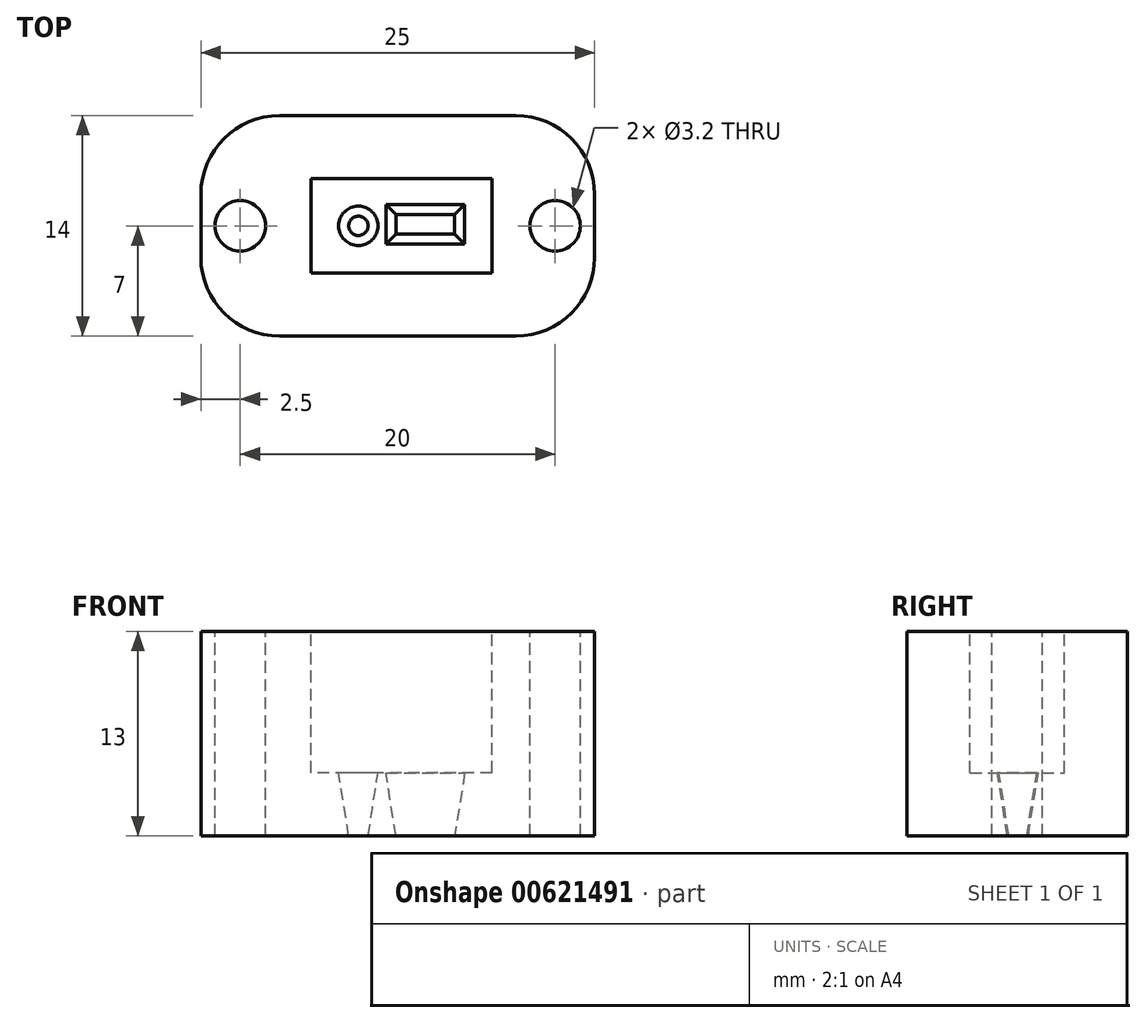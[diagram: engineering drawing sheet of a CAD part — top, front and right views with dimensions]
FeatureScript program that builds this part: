
annotation { "Feature Type Name" : "Feature", "Feature Type Description" : "" }
export const myFeature = defineFeature(function(context is Context, id is Id, definition is map)
    precondition{}
    {
        {
            var Q0;
            Q0=qCreatedBy(makeId("Top.planeOp"),FACE);
            var sketch = newSketch(context, id + "F0", { "sketchPlane" : qUnion([Q0])});
            skLineSegment(sketch, "E0.bottom", {"start": v(6, -3) * mm, "end": v(-5.5, -3) * mm});
            skLineSegment(sketch, "E0.top", {"start": v(6, 3) * mm, "end": v(-5.5, 3) * mm});
            skLineSegment(sketch, "E0.left", {"start": v(6, -3) * mm, "end": v(6, 3) * mm});
            skLineSegment(sketch, "E0.right", {"start": v(-5.5, -3) * mm, "end": v(-5.5, 3) * mm});
            skPoint(sketch, "E0.middle", {"position": v(1.75, 0.1) * mm});
            skLineSegment(sketch, "E1.bottom", {"start": v(12.5, -7) * mm, "end": v(-12.5, -7) * mm});
            skLineSegment(sketch, "E1.top", {"start": v(12.5, 7) * mm, "end": v(-12.5, 7) * mm});
            skLineSegment(sketch, "E1.left", {"start": v(12.5, -7) * mm, "end": v(12.5, 7) * mm});
            skLineSegment(sketch, "E1.right", {"start": v(-12.5, -7) * mm, "end": v(-12.5, 7) * mm});
            skCircle(sketch, "E2", {"center": v(10, 0) * mm, "radius": 1.6 * mm});
            skCircle(sketch, "E3", {"center": v(-10, 0) * mm, "radius": 1.6 * mm});
            skCircle(sketch, "E4", {"center": v(-2.5, 0) * mm, "radius": 1.25 * mm});
            skLineSegment(sketch, "E5.bottom", {"start": v(4.25, -1.16) * mm, "end": v(-0.75, -1.16) * mm});
            skLineSegment(sketch, "E5.top", {"start": v(4.25, 1.34) * mm, "end": v(-0.75, 1.34) * mm});
            skLineSegment(sketch, "E5.left", {"start": v(4.25, -1.16) * mm, "end": v(4.25, 1.34) * mm});
            skLineSegment(sketch, "E5.right", {"start": v(-0.75, -1.16) * mm, "end": v(-0.75, 1.34) * mm});
            skSolve(sketch);
        }
        {
            var Q0;
            Q0=makeQuery(id+"F0.imprint","IMPRINT",FACE,{"disambiguationData":[TD([[makeQuery(id+"F0.imprint","IMPRINT",EDGE,{"derivedFrom":sQuery(id+"F0.wireOp",EDGE,"E0.bottom")}),1.0]])]});
            var Q1;
            Q1=makeQuery(id+"F0.imprint","IMPRINT",FACE,{"disambiguationData":[TD([[makeQuery(id+"F0.imprint","IMPRINT",EDGE,{"derivedFrom":sQuery(id+"F0.wireOp",EDGE,"E0.bottom")}),-1.0]])]});
            var Q2;
            Q2=makeQuery(id+"F0.imprint","IMPRINT",FACE,{"disambiguationData":[TD([[makeQuery(id+"F0.imprint","IMPRINT",EDGE,{"derivedFrom":sQuery(id+"F0.wireOp",EDGE,"E4")}),1.0]])]});
            var Q3;
            Q3=makeQuery(id+"F0.imprint","IMPRINT",FACE,{"disambiguationData":[TD([[makeQuery(id+"F0.imprint","IMPRINT",EDGE,{"derivedFrom":sQuery(id+"F0.wireOp",EDGE,"E5.bottom")}),-1.0]])]});
            extrude(context, id + "F1", {"entities" : qUnion([Q0, Q1, Q2, Q3]), "oppositeDirection" : true, "depth" : 13 * mm, "offsetDistance" : 25 * mm});
        }
        {
            var Q0;
            Q0=makeQuery(id+"F0.imprint","IMPRINT",FACE,{"disambiguationData":[TD([[makeQuery(id+"F0.imprint","IMPRINT",EDGE,{"derivedFrom":sQuery(id+"F0.wireOp",EDGE,"E0.bottom")}),-1.0]])]});
            var Q1;
            Q1=makeQuery(id+"F0.imprint","IMPRINT",FACE,{"disambiguationData":[TD([[makeQuery(id+"F0.imprint","IMPRINT",EDGE,{"derivedFrom":sQuery(id+"F0.wireOp",EDGE,"E4")}),1.0]])]});
            var Q2;
            Q2=makeQuery(id+"F0.imprint","IMPRINT",FACE,{"disambiguationData":[TD([[makeQuery(id+"F0.imprint","IMPRINT",EDGE,{"derivedFrom":sQuery(id+"F0.wireOp",EDGE,"E5.bottom")}),-1.0]])]});
            extrude(context, id + "F2", {"entities" : qUnion([Q0, Q1, Q2]), "operationType" : NewBodyOperationType.REMOVE, "oppositeDirection" : true, "depth" : 9 * mm, "offsetDistance" : 25 * mm});
        }
        {
            var Q0;
            Q0=makeQuery(id+"F2.boolean.opBoolean","COPY",FACE,{"derivedFrom":makeQuery(id+"F2.opExtrude","CAP_FACE",FACE,{"disambiguationData":[OSD([sQuery(id+"F0.wireOp",EDGE,"E0.bottom"),sQuery(id+"F0.wireOp",EDGE,"E0.top"),sQuery(id+"F0.wireOp",EDGE,"E0.left"),sQuery(id+"F0.wireOp",EDGE,"E0.right")])],"isStart":false})});
            var sketch = newSketch(context, id + "F3", { "sketchPlane" : qUnion([Q0])});
            skCircle(sketch, "E6.0", {"center": v(-2.5, 0) * mm, "radius": 1.25 * mm});
            skLineSegment(sketch, "E7.0", {"start": v(4.25, -1.16) * mm, "end": v(-0.75, -1.16) * mm});
            skPoint(sketch, "E8.0", {"position": v(4.25, 0.1) * mm});
            skLineSegment(sketch, "E9.0", {"start": v(4.25, -1.16) * mm, "end": v(4.25, 1.34) * mm});
            skLineSegment(sketch, "E10.0", {"start": v(4.25, 1.34) * mm, "end": v(-0.75, 1.34) * mm});
            skLineSegment(sketch, "E11.0", {"start": v(-0.75, -1.16) * mm, "end": v(-0.75, 1.34) * mm});
            skSolve(sketch);
        }
        {
            var Q0;
            Q0=makeQuery(id+"F3.imprint","IMPRINT",FACE,{"disambiguationData":[TD([[makeQuery(id+"F3.imprint","IMPRINT",EDGE,{"derivedFrom":sQuery(id+"F3.wireOp",EDGE,"E7.0")}),-1.0]])]});
            var Q1;
            Q1=makeQuery(id+"F3.imprint","IMPRINT",FACE,{"disambiguationData":[TD([[makeQuery(id+"F3.imprint","IMPRINT",EDGE,{"derivedFrom":sQuery(id+"F3.wireOp",EDGE,"E6.0")}),1.0]])]});
            extrude(context, id + "F4", {"entities" : qUnion([Q0, Q1]), "operationType" : NewBodyOperationType.REMOVE, "oppositeDirection" : true, "depth" : 5 * mm, "offsetDistance" : 25 * mm, "hasDraft" : true, "draftAngle" : 9 * degree, "draftPullDirection" : true});
        }
        {
            var Q0;
            Q0=makeQuery(id+"F1.opExtrude","SWEPT_EDGE",EDGE,{"disambiguationData":[OSD([sQuery(id+"F0.wireOp",EDGE,"E1.top"),sQuery(id+"F0.wireOp",EDGE,"E1.right")])]});
            var Q1;
            Q1=makeQuery(id+"F1.opExtrude","SWEPT_EDGE",EDGE,{"disambiguationData":[OSD([sQuery(id+"F0.wireOp",EDGE,"E1.bottom"),sQuery(id+"F0.wireOp",EDGE,"E1.left")])]});
            var Q2;
            Q2=makeQuery(id+"F1.opExtrude","SWEPT_EDGE",EDGE,{"disambiguationData":[OSD([sQuery(id+"F0.wireOp",EDGE,"E1.top"),sQuery(id+"F0.wireOp",EDGE,"E1.left")])]});
            var Q3;
            Q3=makeQuery(id+"F1.opExtrude","SWEPT_EDGE",EDGE,{"disambiguationData":[OSD([sQuery(id+"F0.wireOp",EDGE,"E1.bottom"),sQuery(id+"F0.wireOp",EDGE,"E1.right")])]});
            fillet(context, id + "F5", {"entities" : qUnion([Q0, Q1, Q2, Q3]), "radius" : 5 * mm, "tangentPropagation" : true, "allowEdgeOverflow" : false});
        }
    });
